# Revit family: Furniture_Other-Furniture_Hags_Rosenlund-Bicycle-rack
name_source: partatom
category: Furniture
revit_build: Autodesk Revit 2018 (Build: 20190510_1515(x64)
units: mm (PartAtom-declared; Revit-internal decimal feet)

## family parameters
Always vertical = Yes
Cut with Voids When Loaded = No
OmniClass Number = 23.11.27.00
OmniClass Title = Landscaping
Room Calculation Point = No
Shared = No
Work Plane-Based = No

## types (5) — shared parameters
BIMobject category = Other Furniture
Description = Rosenlund Bicycle Stand
Edition number = 1
IFC Classification = Object
Manufacturer = Hags
Manufacturer name = HAGS
OmniClass Code = 23-11 27 00
OmniClass Description = Landscaping
Product Guid = 217313c8-4e35-4501-a999-1e0ddd619f57
Product SKU = Rosenlund_Bicycle_rack
Product data url = https://bimobject.com
Product name = Rosenlund Bicycle Stand
Product url = https://hags.se
QR code = https://bimobject.com
URL = https://www.hags.com
Uniclass 1.4 Code = JN
Uniclass 1.4 Description = Furniture/Equipment

## per-type parameters (varying)
| type | Construction material | Model |
| 8079169 Galvanized | Hags - Steel - Galvanized | 8079169 |
| 8079171 Red | Hags - Steel - Powder coated - Red | 8079171 |
| 8079172 Green | Hags - Steel - Powder coated - Green | 8079172 |
| 8079173 Blue | Hags - Steel - Powder coated - Blue | 8079173 |
| 8079170 Gray | Hags - Steel - Powder coated - Gray | 8079170 |

## geometry (parser evidence)
native form markers: Sweep x3
no freeform markers — native parametric forms only
